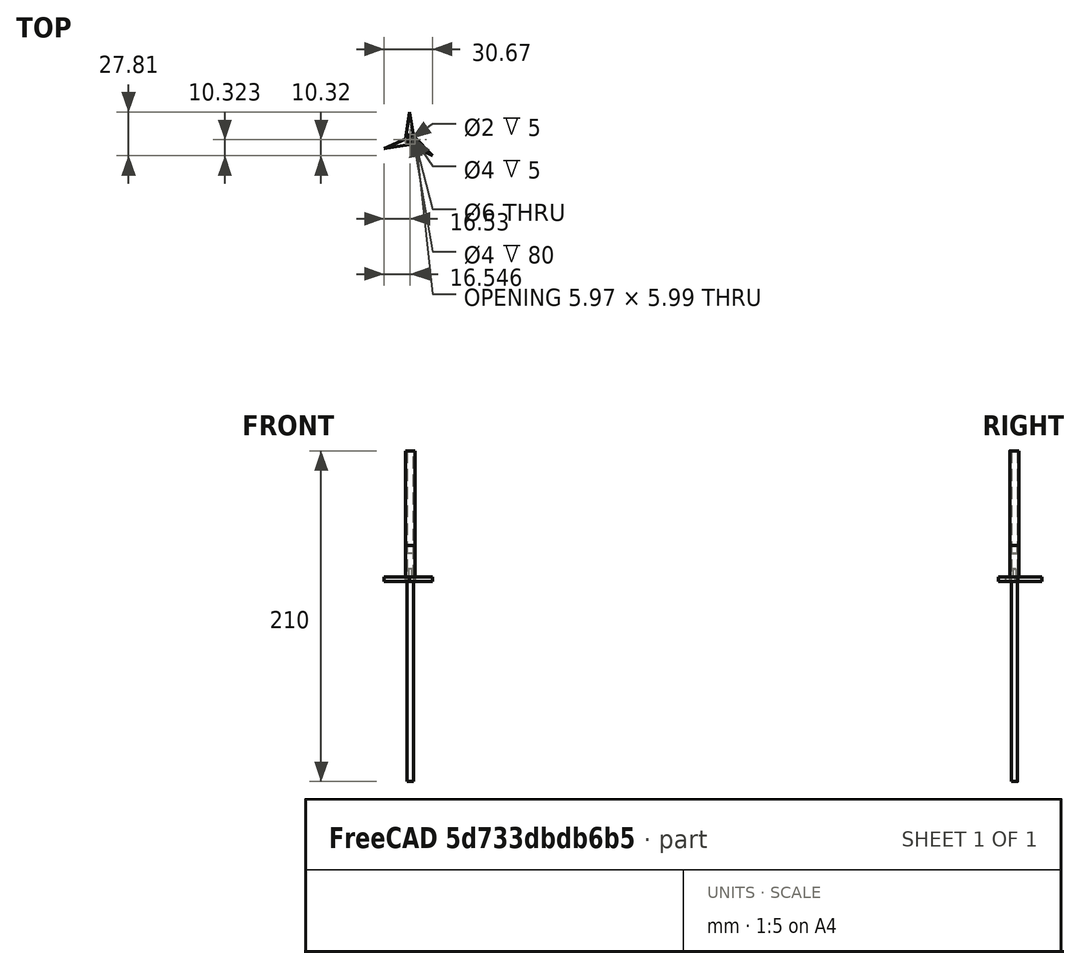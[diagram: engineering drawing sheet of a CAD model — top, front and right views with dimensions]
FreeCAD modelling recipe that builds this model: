
FCSTD DOCUMENT  (FreeCAD 0.19R24366 (Git))
Label: Prop_uxcell_prop_shaft
License: All rights reserved
LicenseURL: http://en.wikipedia.org/wiki/All_rights_reserved
objects: Sketcher::SketchObject×6, Part::Extrusion×3, App::Part×3, PartDesign::Pocket×2, Mesh::Feature×1, PartDesign::Pad×1, PartDesign::Body×1
note: 16 computed .brp shape members not serialized (recipe doc carries the construction recipe); baked Part::Feature solids carry a one-line shape summary decoded from their .brp

FEATURE [Mesh::Feature] driveshaft
FEATURE [Sketcher::SketchObject] Sketch
  FullyConstrained = true
  sketch-geometry (2):
    g0: Circle CenterX=0 CenterY=0 CenterZ=0 NormalX=0 NormalY=0 NormalZ=1 AngleXU=0 Radius=3
    g1: Circle CenterX=0 CenterY=0 CenterZ=0 NormalX=0 NormalY=0 NormalZ=1 AngleXU=0 Radius=2
  constraints (4):
    c: Coincident(g0,g1)
    c: Coincident(g0,g-1)
    c: Diameter(g1) = 4
    c: Diameter(g0) = 6
FEATURE [Part::Extrusion] Extrude  label="PropShaftSleeve001"
  Base = -> Sketch
  Dir = (0,0,1)
  DirMode = 0
  FaceMakerClass = Part::FaceMakerBullseye
  LengthFwd = 80
  LengthRev = 0
  Solid = true
  Symmetric = false
FEATURE [App::Part] Part  label="PropShaftSleeve"
  Group = -> [Sketch,Extrude]
  Origin = -> Origin
FEATURE [Sketcher::SketchObject] Sketch001
  FullyConstrained = false
  sketch-geometry (8):
    g0: Circle CenterX=0 CenterY=0 CenterZ=0 NormalX=0 NormalY=0 NormalZ=1 AngleXU=0 Radius=3
    g1: LineSegment StartX=-2.96858 StartY=0.433018 StartZ=0 EndX=-0.480038 EndY=17.4934 EndZ=0
    g2: LineSegment StartX=2.15757 StartY=2.08444 StartZ=0 EndX=-0.480038 EndY=17.4934 EndZ=0
    g3: LineSegment StartX=-2.96858 StartY=0.433018 StartZ=0 EndX=-16.5261 EndY=-5.75668 EndZ=0
    g4: LineSegment StartX=-16.5261 StartY=-5.75668 StartZ=0 EndX=-0.463294 EndY=-3.11641 EndZ=0
    g5: LineSegment StartX=-0.463294 StartY=-3.11641 StartZ=0 EndX=14.1368 EndY=-10.3151 EndZ=0
    g6: LineSegment StartX=14.1368 StartY=-10.3151 StartZ=0 EndX=2.15757 EndY=2.08444 EndZ=0
    g7: Circle CenterX=0 CenterY=0 CenterZ=0 NormalX=0 NormalY=0 NormalZ=1 AngleXU=0 Radius=17.5
  constraints (19):
    c: Coincident(g0,g-1)
    c: Diameter(g0) = 6
    c: PointOnObject(g1,g0)
    c: PointOnObject(g2,g0)
    c: Coincident(g2,g1)
    c: Coincident(g4,g3)
    c: Coincident(g4,g5)
    c: Tangent(g5,g0)
    c: Tangent(g4,g0)
    c: Coincident(g3,g1)
    c: Coincident(g2,g6)
    c: Coincident(g7,g0)
    c: PointOnObject(g5,g7)
    c: PointOnObject(g3,g7)
    c: PointOnObject(g1,g7)
    c: Coincident(g6,g5)
    c: Diameter(g7) = 35
    c: Tangent(g0,g1,g1) = 1.5708
    c: Tangent(g6,g0,g2) = -1.5708
FEATURE [Part::Extrusion] Extrude001  label="PropMock"
  Base = -> Sketch001
  Dir = (0,0,-1)
  DirMode = 0
  FaceMakerClass = Part::FaceMakerBullseye
  LengthFwd = 3
  LengthRev = 0
  Solid = true
  Symmetric = false
FEATURE [Sketcher::SketchObject] Sketch002
  FullyConstrained = true
  sketch-geometry (1):
    g0: Circle CenterX=0 CenterY=0 CenterZ=0 NormalX=0 NormalY=0 NormalZ=1 AngleXU=0 Radius=2
  constraints (2):
    c: Coincident(g0,g-1)
    c: Diameter(g0) = 4
FEATURE [Part::Extrusion] Extrude002  label="PropShaft"
  Base = -> Sketch002
  Dir = (0,0,-1)
  DirMode = 0
  FaceMakerClass = Part::FaceMakerBullseye
  LengthFwd = 130
  LengthRev = 0
  Solid = true
  Symmetric = false
FEATURE [App::Part] Part001  label="PropAndShaft"
  Group = -> [Sketch001,Extrude001,Sketch002,Extrude002]
  Origin = -> Origin001
FEATURE [Sketcher::SketchObject] Sketch003
  FullyConstrained = true
  MapMode = 5
  Support = -> [XY_Plane003]
  sketch-geometry (1):
    g0: Circle CenterX=0 CenterY=0 CenterZ=0 NormalX=0 NormalY=0 NormalZ=1 AngleXU=0 Radius=3
  constraints (2):
    c: Coincident(g0,g-1)
    c: Diameter(g0) = 6
FEATURE [PartDesign::Pad] Pad
  Direction = (1,1,1)
  Length = 20
  Length2 = 100
  Profile = -> Sketch003
  Type = 0
FEATURE [Sketcher::SketchObject] Sketch004
  FullyConstrained = true
  MapMode = 5
  Placement = pos=(0,0,20) rot=(0,0,1;0rad)
  Support = -> [Pad]
  sketch-geometry (1):
    g0: Circle CenterX=0 CenterY=0 CenterZ=0 NormalX=0 NormalY=0 NormalZ=1 AngleXU=0 Radius=2
  constraints (2):
    c: Coincident(g0,g-1)
    c: Diameter(g0) = 4
FEATURE [PartDesign::Pocket] Pocket
  BaseFeature = -> Pad
  Length = 5
  Length2 = 100
  Profile = -> Sketch004
  Type = 0
FEATURE [Sketcher::SketchObject] Sketch005
  FullyConstrained = true
  MapMode = 5
  Placement = pos=(0,0,0) rot=(1,0,0;3.14159rad)
  Support = -> [Pocket]
  sketch-geometry (1):
    g0: Circle CenterX=0 CenterY=0 CenterZ=0 NormalX=0 NormalY=0 NormalZ=1 AngleXU=0 Radius=1
  constraints (2):
    c: Coincident(g0,g-1)
    c: Diameter(g0) = 2
FEATURE [PartDesign::Pocket] Pocket001
  BaseFeature = -> Pocket
  Length = 5
  Length2 = 100
  Profile = -> Sketch005
  Type = 0
FEATURE [PartDesign::Body] Body
  Group = -> [Sketch003,Pad,Sketch004,Pocket,Sketch005,Pocket001]
  Origin = -> Origin003
  Tip = -> Pocket001
FEATURE [App::Part] Part002  label="ShaftConnectorTemp"
  Group = -> [Body]
  Origin = -> Origin002
